# Revit family: DLB090023-FR
name_source: partatom
category: Appareils sanitaires
revit_build: Autodesk Revit 2015 (Build: 20140606_1530(x64)
units: mm (PartAtom-declared; Revit-internal decimal feet)

## types (1)
- Type 1
    Commentaires du type = WC à poser
    Descriptif = WC à poser au sol.
Design pur et élégant.
Inox 304 bactériostatique.
Épaisseur Inox : 1,5 mm.
Cuvette emboutie, sans soudures, pour un entretien facile et une meilleure hygiène.
Intérieur de la cuvette poli et bords arrondis pour un nettoyage aisé.
Rebord à effet d’eau intégré.
Arrivée d’eau horizontale Ø 55 mm.
Évacuation d’eau horizontale ou verticale Ø 100 mm. Livré avec pipe PVC.
Économie d’eau : fonctionne avec 4 litres d'eau et plus.
Perçages pour la fixation de l’abattant. Livré avec cache-trous en Inox pour utilisation sans abattant.
Installation rapide et facile : 2 trappes de visite avec vis antivol TORX.
Marquage CE. Conforme à la norme EN 997 pour une chasse d’eau 4 litres.
Poids : 14 kg.
    Description = DELABIE, fabricant français, est le leader européen de l'équipement sanitaire pour les établissements recevant du public. Robinetteries, solutions pour personnes à mobilité réduite, appareils sanitaires, destinés aux écoles, lieux de loisirs, bureaux, hôpitaux, aéroports, ...
    Fabricant = DELABIE
    Famille de produits = WC
    Finition = Inox 304 poli satiné
    Hauteur = 400 mm
    Largeur = 360 mm
    Lien CCTP = http://www.delabie.fr
    Lien certification = http://www.delabie.fr
    Lien fiche produit = http://www.delabie.fr
    Lien notice d'installation = http://www.delabie.fr
    Modèle = S21 P
    Nom = 110300
    Polantis code = DLB090023
    Profondeur = 580 mm
    Radius (Entrée) = 55 mm  [stored 0.180446 ft]
    Radius (Sortie) = 100 mm  [stored 0.328084 ft]
    URL = http://www.delabie.fr

note: [stored X ft] marks values corroborated as IEEE doubles in the binary element streams (Revit-internal decimal feet)

## geometry (parser evidence)
native form markers: Sweep x4
no freeform markers — native parametric forms only
